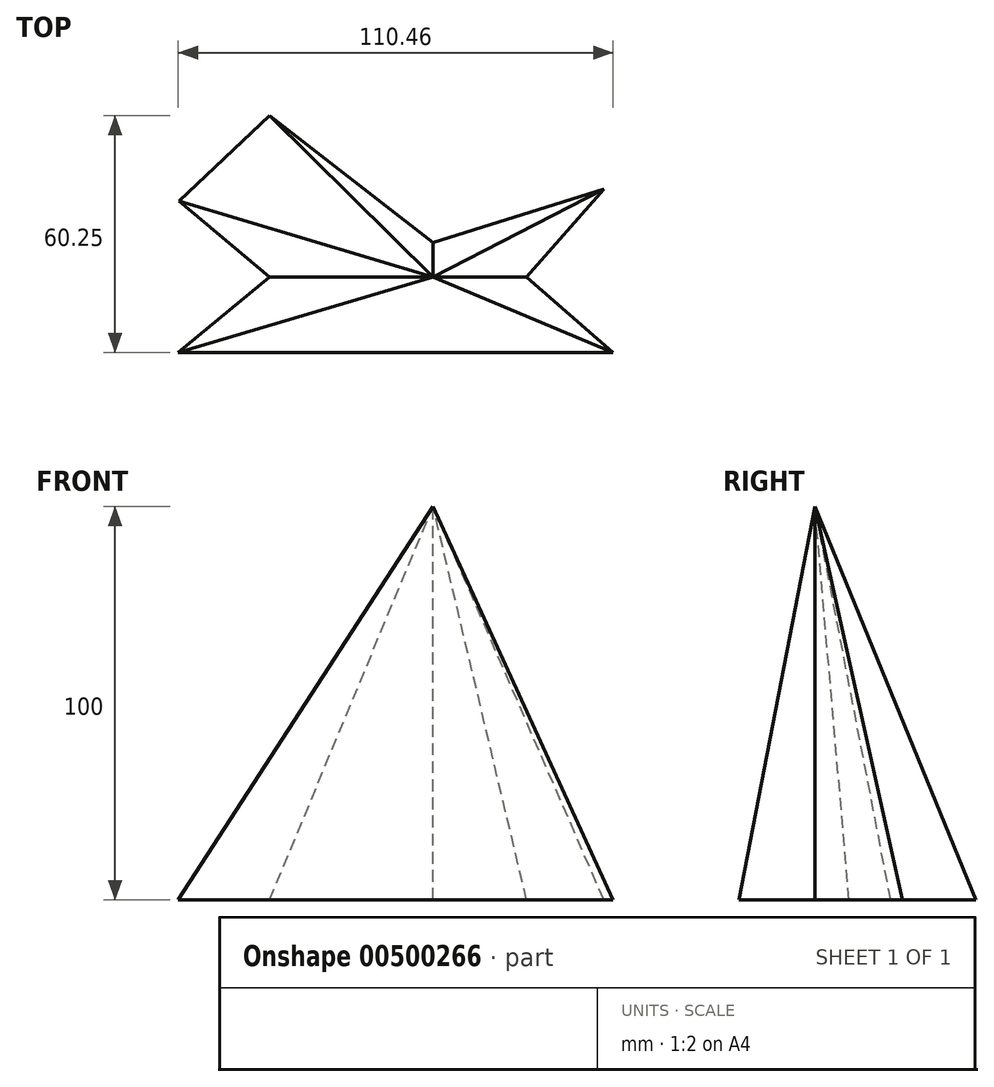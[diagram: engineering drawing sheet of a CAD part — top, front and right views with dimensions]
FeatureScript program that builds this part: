
annotation { "Feature Type Name" : "Feature", "Feature Type Description" : "" }
export const myFeature = defineFeature(function(context is Context, id is Id, definition is map)
    precondition{}
    {
        {
            var Q0;
            Q0=qCreatedBy(makeId("Top.planeOp"),FACE);
            var sketch = newSketch(context, id + "F0", { "sketchPlane" : qUnion([Q0])});
            skLineSegment(sketch, "E0", {"start": v(-41.49, 0) * mm, "end": v(-64.74, -19.3) * mm});
            skLineSegment(sketch, "E1", {"start": v(-41.49, 0) * mm, "end": v(-64.48, 19.3) * mm});
            skLineSegment(sketch, "E2", {"start": v(-64.74, -19.3) * mm, "end": v(45.72, -19.3) * mm});
            skLineSegment(sketch, "E3", {"start": v(45.72, -19.3) * mm, "end": v(23.78, 0) * mm});
            skLineSegment(sketch, "E4", {"start": v(23.78, 0) * mm, "end": v(43.4, 22.3) * mm});
            skLineSegment(sketch, "E5", {"start": v(43.4, 22.3) * mm, "end": v(0, 8.72) * mm});
            skLineSegment(sketch, "E6", {"start": v(0, 8.72) * mm, "end": v(-41.49, 40.96) * mm});
            skLineSegment(sketch, "E7", {"start": v(-41.49, 40.96) * mm, "end": v(-64.48, 19.3) * mm});
            skSolve(sketch);
        }
        {
            var Q0;
            Q0=qCreatedBy(makeId("Top.planeOp"),FACE);
            cPlane(context, id + "F1", {"entities" : qUnion([Q0]), "cplaneType" : CPlaneType.OFFSET, "offset" : 100 * mm, "width" : 150 * mm, "height" : 150 * mm});
        }
        {
            var Q0;
            Q0=qCreatedBy(id+"F1.planeOp",FACE);
            var sketch = newSketch(context, id + "F2", { "sketchPlane" : qUnion([Q0])});
            skPoint(sketch, "E8", {"position": v(0, 0) * mm});
            skSolve(sketch);
        }
        {
            var Q0;
            Q0=makeQuery(id+"F0.imprint","IMPRINT",FACE,{"disambiguationData":[TD([[makeQuery(id+"F0.imprint","IMPRINT",EDGE,{"derivedFrom":sQuery(id+"F0.wireOp",EDGE,"E0")}),1.0]])]});
            var Q1;
            Q1=sQuery(id+"F2.wireOp",VERTEX,"E8");
            loft(context, id + "F3", {"sheetProfilesArray" : [{ "sheetProfileEntities" : qUnion([Q0]) }, { "sheetProfileEntities" : qUnion([Q1]) }]});
        }
    });
